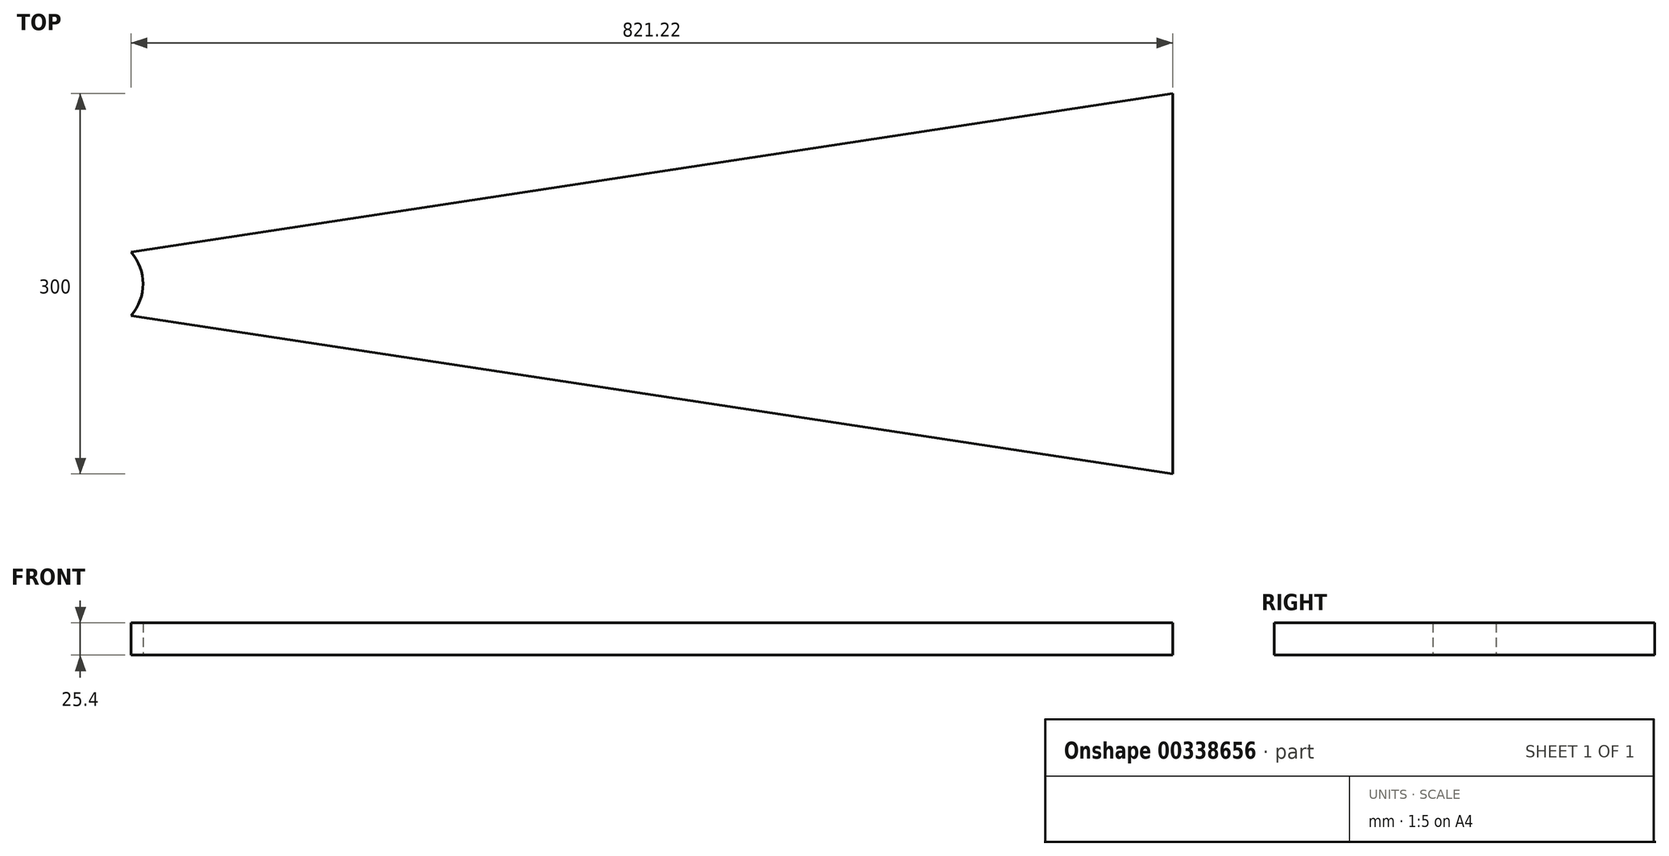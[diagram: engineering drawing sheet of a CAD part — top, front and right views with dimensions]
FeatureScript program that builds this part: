
annotation { "Feature Type Name" : "Feature", "Feature Type Description" : "" }
export const myFeature = defineFeature(function(context is Context, id is Id, definition is map)
    precondition{}
    {
        {
            var Q0;
            Q0=qCreatedBy(makeId("Top.planeOp"),FACE);
            var sketch = newSketch(context, id + "F0", { "sketchPlane" : qUnion([Q0])});
            skArc(sketch, "E0", {"start": v(28.78, -24.97) * mm, "mid": v(38.1, 0) * mm, "end": v(28.78, 24.97) * mm});
            skLineSegment(sketch, "E1", {"start": v(850, 0) * mm, "end": v(850, 150) * mm});
            skLineSegment(sketch, "E2", {"start": v(850, 0) * mm, "end": v(850, -150) * mm});
            skLineSegment(sketch, "E3", {"start": v(850, 150) * mm, "end": v(28.78, 24.97) * mm});
            skLineSegment(sketch, "E4", {"start": v(28.78, -24.97) * mm, "end": v(850, -150) * mm});
            skSolve(sketch);
        }
        {
            var Q0;
            Q0=makeQuery(id+"F0.imprint","IMPRINT",FACE,{"disambiguationData":[TD([[makeQuery(id+"F0.imprint","IMPRINT",EDGE,{"derivedFrom":sQuery(id+"F0.wireOp",EDGE,"E0")}),-1.0]])]});
            extrude(context, id + "F1", {"entities" : qUnion([Q0]), "depth" : 25.4 * mm});
        }
    });
